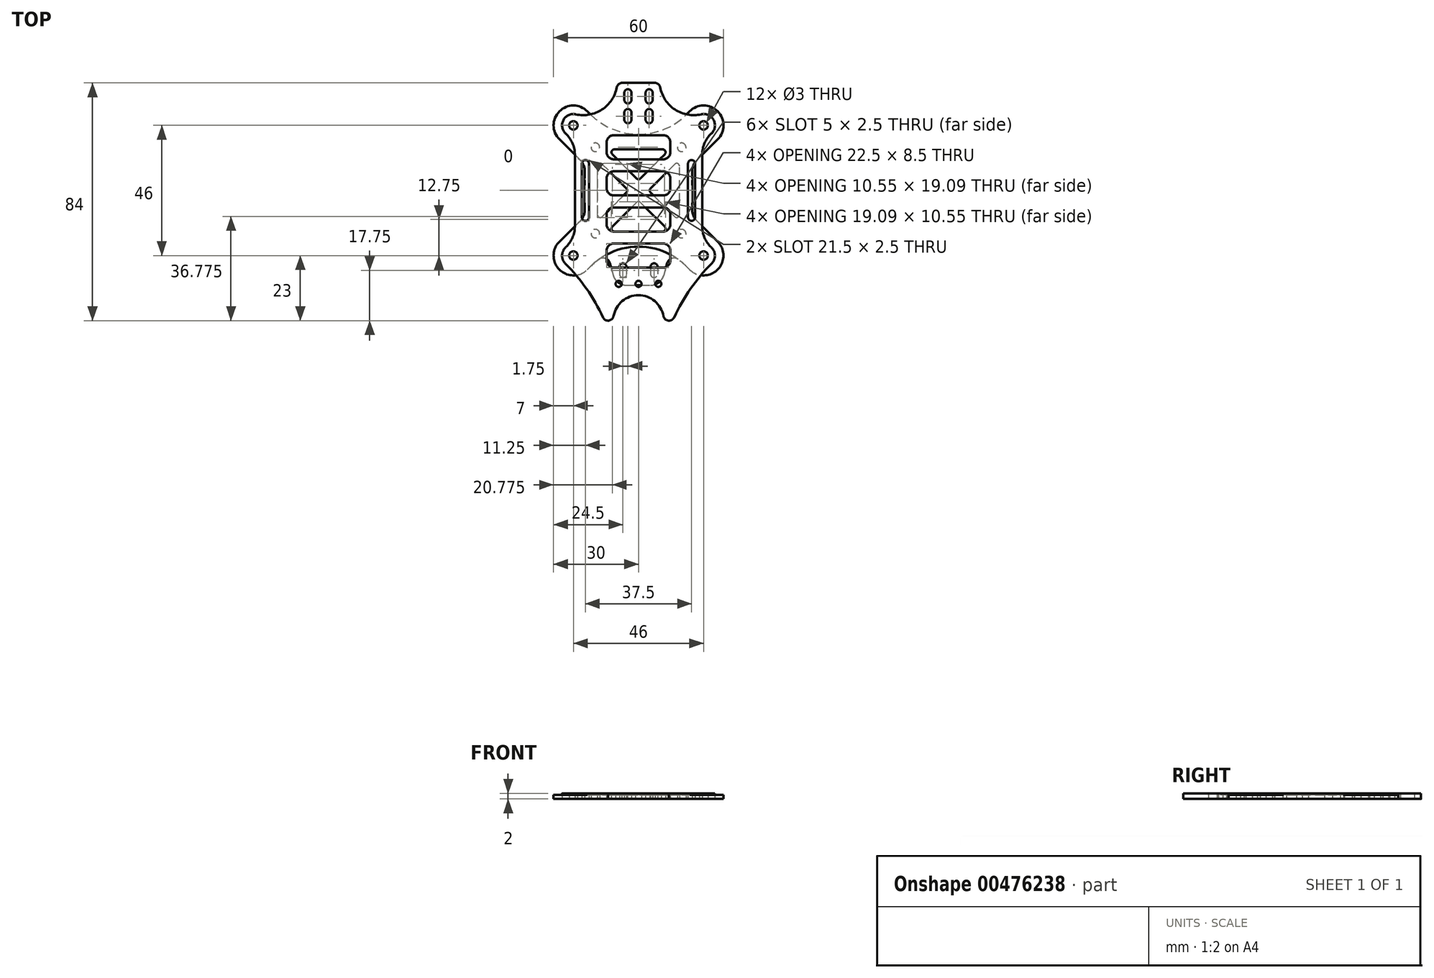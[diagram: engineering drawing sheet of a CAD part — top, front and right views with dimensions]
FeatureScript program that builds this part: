
annotation { "Feature Type Name" : "Feature", "Feature Type Description" : "" }
export const myFeature = defineFeature(function(context is Context, id is Id, definition is map)
    precondition{}
    {
        {
            var Q0;
            Q0=qCreatedBy(makeId("Top.planeOp"),FACE);
            var sketch = newSketch(context, id + "F0", { "sketchPlane" : qUnion([Q0])});
            skCircle(sketch, "E0", {"center": v(-15.25, 15.25) * mm, "radius": 1.52 * mm});
            skCircle(sketch, "E1", {"center": v(15.25, 15.25) * mm, "radius": 1.52 * mm});
            skCircle(sketch, "E2", {"center": v(15.25, -15.25) * mm, "radius": 1.52 * mm});
            skCircle(sketch, "E3", {"center": v(-15.25, -15.25) * mm, "radius": 1.52 * mm});
            skCircle(sketch, "E4", {"center": v(-23, 23) * mm, "radius": 1.5 * mm});
            skCircle(sketch, "E5.MirrorC", {"center": v(23, 23) * mm, "radius": 1.5 * mm});
            skCircle(sketch, "E6.MirrorC", {"center": v(-23, -23) * mm, "radius": 1.5 * mm});
            skCircle(sketch, "E7.MirrorC", {"center": v(23, -23) * mm, "radius": 1.5 * mm});
            skArc(sketch, "E8", {"start": v(-18.05, 27.95) * mm, "mid": v(-27.95, 27.95) * mm, "end": v(-27.95, 18.05) * mm});
            skLineSegment(sketch, "E9", {"start": v(-19, 7.03) * mm, "end": v(-19, -7.03) * mm});
            skLineSegment(sketch, "E10", {"start": v(-18.05, 27.95) * mm, "end": v(-16.97, 26.87) * mm});
            skLineSegment(sketch, "E11", {"start": v(-27.95, 18.05) * mm, "end": v(-20.46, 10.56) * mm});
            skLineSegment(sketch, "E12.MirrorCS", {"start": v(-27.95, -18.05) * mm, "end": v(-20.46, -10.56) * mm});
            skArc(sketch, "E13.MirrorCS", {"start": v(-18.05, -27.95) * mm, "mid": v(-27.95, -27.95) * mm, "end": v(-27.95, -18.05) * mm});
            skLineSegment(sketch, "E14.MirrorCS", {"start": v(-18.05, -27.95) * mm, "end": v(-16.97, -26.87) * mm});
            skLineSegment(sketch, "E15.MirrorCS", {"start": v(18.05, 27.95) * mm, "end": v(16.97, 26.87) * mm});
            skArc(sketch, "E16.MirrorCS", {"start": v(18.05, 27.95) * mm, "mid": v(27.95, 27.95) * mm, "end": v(27.95, 18.05) * mm});
            skLineSegment(sketch, "E17.MirrorCS", {"start": v(27.95, 18.05) * mm, "end": v(20.46, 10.56) * mm});
            skLineSegment(sketch, "E18.MirrorCS", {"start": v(27.95, -18.05) * mm, "end": v(20.46, -10.56) * mm});
            skArc(sketch, "E19.MirrorCS", {"start": v(18.05, -27.95) * mm, "mid": v(27.95, -27.95) * mm, "end": v(27.95, -18.05) * mm});
            skLineSegment(sketch, "E20.MirrorCS", {"start": v(18.05, -27.95) * mm, "end": v(16.97, -26.87) * mm});
            skPoint(sketch, "E21.visualSharp", {"position": v(0, 9.9) * mm});
            skPoint(sketch, "E22.visualSharp", {"position": v(0, -9.9) * mm});
            skArc(sketch, "E22.filletArc", {"start": v(16.97, -26.87) * mm, "mid": v(0, -19.84) * mm, "end": v(-16.97, -26.87) * mm});
            skLineSegment(sketch, "E23", {"start": v(-23, 23) * mm, "end": v(0, 0) * mm, "construction": true});
            skArc(sketch, "E24.filletArc", {"start": v(-16.97, 26.87) * mm, "mid": v(0, 19.84) * mm, "end": v(16.97, 26.87) * mm});
            skPoint(sketch, "E25.visualSharp", {"position": v(-19, 11.8) * mm});
            skArc(sketch, "E25.filletArc", {"start": v(-19, 7.03) * mm, "mid": v(-19.38, 8.94) * mm, "end": v(-20.46, 10.56) * mm});
            skPoint(sketch, "E26.visualSharp", {"position": v(-19, -11.8) * mm});
            skArc(sketch, "E26.filletArc", {"start": v(-20.46, -10.56) * mm, "mid": v(-19.38, -8.94) * mm, "end": v(-19, -7.03) * mm});
            skArc(sketch, "E27.MirrorCS", {"start": v(20.46, -10.56) * mm, "mid": v(19.38, -8.94) * mm, "end": v(19, -7.03) * mm});
            skArc(sketch, "E28.MirrorCS", {"start": v(19, 7.03) * mm, "mid": v(19.38, 8.94) * mm, "end": v(20.46, 10.56) * mm});
            skPoint(sketch, "E29.MirrorP", {"position": v(19, -11.8) * mm});
            skLineSegment(sketch, "E30.MirrorCS", {"start": v(19, 7.03) * mm, "end": v(19, -7.03) * mm});
            skPoint(sketch, "E31.MirrorP", {"position": v(21.5, -11.8) * mm});
            skPoint(sketch, "E32.MirrorP", {"position": v(21.5, 11.8) * mm});
            skPoint(sketch, "E33.MirrorP", {"position": v(19, 11.8) * mm});
            skLineSegment(sketch, "E34", {"start": v(0, 0) * mm, "end": v(23, -23) * mm, "construction": true});
            skLineSegment(sketch, "E35", {"start": v(23, 23) * mm, "end": v(-23, -23) * mm, "construction": true});
            skLineSegment(sketch, "E36.0", {"start": v(0.7, -4.24) * mm, "end": v(9.26, -12.8) * mm});
            skLineSegment(sketch, "E36.1", {"start": v(-12.8, 9.26) * mm, "end": v(-4.24, 0.7) * mm});
            skLineSegment(sketch, "E37.0", {"start": v(-9.26, 12.8) * mm, "end": v(-0.7, 4.24) * mm});
            skLineSegment(sketch, "E38.0", {"start": v(4.24, -0.7) * mm, "end": v(12.8, -9.26) * mm});
            skLineSegment(sketch, "E39.MirrorCS", {"start": v(9.26, 12.8) * mm, "end": v(0.7, 4.24) * mm});
            skLineSegment(sketch, "E40.MirrorCS", {"start": v(12.8, 9.26) * mm, "end": v(4.24, 0.7) * mm});
            skLineSegment(sketch, "E41.MirrorCS", {"start": v(-0.7, -4.24) * mm, "end": v(-9.26, -12.8) * mm});
            skLineSegment(sketch, "E42.MirrorCS", {"start": v(-4.24, -0.7) * mm, "end": v(-12.8, -9.26) * mm});
            skPoint(sketch, "E43.orphan", {"position": v(-1.77, -1.77) * mm});
            skPoint(sketch, "E44.orphan", {"position": v(1.77, -1.77) * mm});
            skLineSegment(sketch, "E45", {"start": v(-8.55, 14.5) * mm, "end": v(8.55, 14.5) * mm});
            skLineSegment(sketch, "E46", {"start": v(-14.5, 8.55) * mm, "end": v(-14.5, -8.55) * mm});
            skLineSegment(sketch, "E47", {"start": v(-8.55, -14.5) * mm, "end": v(8.55, -14.5) * mm});
            skLineSegment(sketch, "E48", {"start": v(14.5, -8.55) * mm, "end": v(14.5, 8.55) * mm});
            skPoint(sketch, "E49.visualSharp", {"position": v(-14.5, 10.96) * mm});
            skArc(sketch, "E49.filletArc", {"start": v(-12.8, 9.26) * mm, "mid": v(-13.88, 9.47) * mm, "end": v(-14.5, 8.55) * mm});
            skPoint(sketch, "E50.visualSharp", {"position": v(-14.5, -10.96) * mm});
            skArc(sketch, "E50.filletArc", {"start": v(-14.5, -8.55) * mm, "mid": v(-13.88, -9.47) * mm, "end": v(-12.8, -9.26) * mm});
            skPoint(sketch, "E51.visualSharp", {"position": v(-3.54, 0) * mm});
            skArc(sketch, "E51.filletArc", {"start": v(-4.24, -0.7) * mm, "mid": v(-3.95, 0) * mm, "end": v(-4.24, 0.7) * mm});
            skPoint(sketch, "E52.visualSharp", {"position": v(0, -3.54) * mm});
            skArc(sketch, "E52.filletArc", {"start": v(0.7, -4.24) * mm, "mid": v(0, -3.95) * mm, "end": v(-0.7, -4.24) * mm});
            skPoint(sketch, "E53.visualSharp", {"position": v(-10.96, -14.5) * mm});
            skArc(sketch, "E53.filletArc", {"start": v(-9.26, -12.8) * mm, "mid": v(-9.47, -13.88) * mm, "end": v(-8.55, -14.5) * mm});
            skPoint(sketch, "E54.visualSharp", {"position": v(10.96, -14.5) * mm});
            skArc(sketch, "E54.filletArc", {"start": v(8.55, -14.5) * mm, "mid": v(9.47, -13.88) * mm, "end": v(9.26, -12.8) * mm});
            skPoint(sketch, "E55.visualSharp", {"position": v(14.5, -10.96) * mm});
            skArc(sketch, "E55.filletArc", {"start": v(12.8, -9.26) * mm, "mid": v(13.88, -9.47) * mm, "end": v(14.5, -8.55) * mm});
            skPoint(sketch, "E56.visualSharp", {"position": v(14.5, 10.96) * mm});
            skArc(sketch, "E56.filletArc", {"start": v(14.5, 8.55) * mm, "mid": v(13.88, 9.47) * mm, "end": v(12.8, 9.26) * mm});
            skPoint(sketch, "E57.visualSharp", {"position": v(3.54, 0) * mm});
            skArc(sketch, "E57.filletArc", {"start": v(4.24, 0.7) * mm, "mid": v(3.95, 0) * mm, "end": v(4.24, -0.7) * mm});
            skPoint(sketch, "E58.visualSharp", {"position": v(0, 3.54) * mm});
            skArc(sketch, "E58.filletArc", {"start": v(-0.7, 4.24) * mm, "mid": v(0, 3.95) * mm, "end": v(0.7, 4.24) * mm});
            skPoint(sketch, "E59.visualSharp", {"position": v(-10.96, 14.5) * mm});
            skArc(sketch, "E59.filletArc", {"start": v(-8.55, 14.5) * mm, "mid": v(-9.47, 13.88) * mm, "end": v(-9.26, 12.8) * mm});
            skPoint(sketch, "E60.visualSharp", {"position": v(10.96, 14.5) * mm});
            skArc(sketch, "E60.filletArc", {"start": v(9.26, 12.8) * mm, "mid": v(9.47, 13.88) * mm, "end": v(8.55, 14.5) * mm});
            skLineSegment(sketch, "E61", {"start": v(-11, -22.5) * mm, "end": v(-9, -29.82) * mm});
            skLineSegment(sketch, "E62", {"start": v(-4.18, -33.5) * mm, "end": v(4.18, -33.5) * mm});
            skLineSegment(sketch, "E63", {"start": v(9, -29.82) * mm, "end": v(11, -22.5) * mm});
            skPoint(sketch, "E64.visualSharp", {"position": v(-8, -33.5) * mm});
            skArc(sketch, "E64.filletArc", {"start": v(-9, -29.82) * mm, "mid": v(-7.22, -32.47) * mm, "end": v(-4.18, -33.5) * mm});
            skPoint(sketch, "E65.visualSharp", {"position": v(8, -33.5) * mm});
            skArc(sketch, "E65.filletArc", {"start": v(4.18, -33.5) * mm, "mid": v(7.22, -32.47) * mm, "end": v(9, -29.82) * mm});
            skLineSegment(sketch, "E66", {"start": v(-5.5, -27) * mm, "end": v(-5.5, -29.5) * mm, "construction": true});
            skArc(sketch, "E67.0.startCap", {"start": v(-6.75, -27) * mm, "mid": v(-5.5, -25.75) * mm, "end": v(-4.25, -27) * mm});
            skArc(sketch, "E67.0.endCap", {"start": v(-4.25, -29.5) * mm, "mid": v(-5.5, -30.75) * mm, "end": v(-6.75, -29.5) * mm});
            skLineSegment(sketch, "E67.0.left", {"start": v(-4.25, -27) * mm, "end": v(-4.25, -29.5) * mm});
            skLineSegment(sketch, "E67.0.right", {"start": v(-6.75, -27) * mm, "end": v(-6.75, -29.5) * mm});
            skArc(sketch, "E68.MirrorCS", {"start": v(6.75, -27) * mm, "mid": v(5.5, -25.75) * mm, "end": v(4.25, -27) * mm});
            skArc(sketch, "E69.MirrorCS", {"start": v(4.25, -29.5) * mm, "mid": v(5.5, -30.75) * mm, "end": v(6.75, -29.5) * mm});
            skLineSegment(sketch, "E70.MirrorCS", {"start": v(5.5, -27) * mm, "end": v(5.5, -29.5) * mm, "construction": true});
            skLineSegment(sketch, "E71.MirrorCS", {"start": v(4.25, -27) * mm, "end": v(4.25, -29.5) * mm});
            skLineSegment(sketch, "E72.MirrorCS", {"start": v(6.75, -27) * mm, "end": v(6.75, -29.5) * mm});
            skSolve(sketch);
        }
        {
            var Q0;
            Q0=makeQuery(id+"F0.imprint","IMPRINT",FACE,{"disambiguationData":[TD([[makeQuery(id+"F0.imprint","IMPRINT",EDGE,{"derivedFrom":sQuery(id+"F0.wireOp",EDGE,"E0")}),-1.0]])]});
            extrude(context, id + "F1", {"entities" : qUnion([Q0]), "depth" : 1.5 * mm});
        }
        {
            var Q0;
            Q0 = qSketchRegion(id + "F0", true);
            extrude(context, id + "F2", {"entities" : qUnion([Q0]), "depth" : 1.5 * mm, "offsetDistance" : 25 * mm});
        }
        {
            var Q0;
            Q0=makeQuery(id+"F2.opExtrude","SWEPT_EDGE",EDGE,{"disambiguationData":[OSD([sQuery(id+"F0.wireOp",EDGE,"E22.filletArc"),sQuery(id+"F0.wireOp",EDGE,"E61")])]});
            var Q1;
            Q1=makeQuery(id+"F2.opExtrude","SWEPT_EDGE",EDGE,{"disambiguationData":[OSD([sQuery(id+"F0.wireOp",EDGE,"E22.filletArc"),sQuery(id+"F0.wireOp",EDGE,"E63")])]});
            fillet(context, id + "F3", {"entities" : qUnion([Q0, Q1]), "radius" : 2.5 * mm, "tangentPropagation" : true, "allowEdgeOverflow" : false});
        }
        {
            var Q0;
            Q0=qCreatedBy(makeId("Top.planeOp"),FACE);
            var sketch = newSketch(context, id + "F4", { "sketchPlane" : qUnion([Q0])});
            skCircle(sketch, "E73", {"center": v(-23, 23) * mm, "radius": 1.5 * mm});
            skLineSegment(sketch, "E74", {"start": v(-23, 23) * mm, "end": v(0, 0) * mm, "construction": true});
            skLineSegment(sketch, "E75", {"start": v(-22.5, 12.72) * mm, "end": v(-22.5, 0) * mm});
            skArc(sketch, "E76.filletArc", {"start": v(-22.5, 12.72) * mm, "mid": v(-23.34, 16.73) * mm, "end": v(-25.71, 20.06) * mm});
            skLineSegment(sketch, "E77", {"start": v(0, 0) * mm, "end": v(0, 0) * mm});
            skLineSegment(sketch, "E78.MirrorCS", {"start": v(22.5, 12.72) * mm, "end": v(22.5, 0) * mm});
            skCircle(sketch, "E79.MirrorC", {"center": v(23, 23) * mm, "radius": 1.5 * mm});
            skLineSegment(sketch, "E80.MirrorCS", {"start": v(23, 23) * mm, "end": v(0, 0) * mm, "construction": true});
            skArc(sketch, "E81.MirrorCS", {"start": v(22.5, 12.72) * mm, "mid": v(23.34, 16.73) * mm, "end": v(25.71, 20.06) * mm});
            skLineSegment(sketch, "E82.MirrorCS", {"start": v(0, 36) * mm, "end": v(0, 0) * mm, "construction": true});
            skArc(sketch, "E83.MirrorCS", {"start": v(-22.5, -12.72) * mm, "mid": v(-23.34, -16.73) * mm, "end": v(-25.71, -20.06) * mm});
            skLineSegment(sketch, "E84.MirrorCS", {"start": v(-22.5, -12.72) * mm, "end": v(-22.5, 0) * mm});
            skLineSegment(sketch, "E85.MirrorCS", {"start": v(22.5, -12.72) * mm, "end": v(22.5, 0) * mm});
            skArc(sketch, "E86.MirrorCS", {"start": v(22.5, -12.72) * mm, "mid": v(23.34, -16.73) * mm, "end": v(25.71, -20.06) * mm});
            skArc(sketch, "E87.MirrorCS", {"start": v(25.83, -25.83) * mm, "mid": v(27, -22.92) * mm, "end": v(25.71, -20.06) * mm});
            skCircle(sketch, "E88.MirrorC", {"center": v(-23, -23) * mm, "radius": 1.5 * mm});
            skCircle(sketch, "E89.MirrorC", {"center": v(23, -23) * mm, "radius": 1.5 * mm});
            skLineSegment(sketch, "E90", {"start": v(0, 0) * mm, "end": v(-72.48, -72.48) * mm, "construction": true});
            skCircle(sketch, "E91", {"center": v(-72.48, -72.48) * mm, "radius": 65.25 * mm, "construction": true});
            skArc(sketch, "E92", {"start": v(-12.05, -46) * mm, "mid": v(-18, -35.27) * mm, "end": v(-25.83, -25.83) * mm});
            skArc(sketch, "E93", {"start": v(-25.83, -25.83) * mm, "mid": v(-27, -22.92) * mm, "end": v(-25.71, -20.06) * mm});
            skArc(sketch, "E94.MirrorCS", {"start": v(12.05, -46) * mm, "mid": v(18, -35.27) * mm, "end": v(25.83, -25.83) * mm});
            skLineSegment(sketch, "E95", {"start": v(-12.05, -46) * mm, "end": v(-8.97, -46) * mm});
            skLineSegment(sketch, "E96.trimOffspring", {"start": v(8.97, -46) * mm, "end": v(12.05, -46) * mm});
            skLineSegment(sketch, "E97", {"start": v(-3.75, 27.5) * mm, "end": v(-3.75, 25) * mm, "construction": true});
            skArc(sketch, "E98.0.startCap", {"start": v(-5, 27.5) * mm, "mid": v(-3.75, 28.75) * mm, "end": v(-2.5, 27.5) * mm});
            skArc(sketch, "E98.0.endCap", {"start": v(-2.5, 25) * mm, "mid": v(-3.75, 23.75) * mm, "end": v(-5, 25) * mm});
            skLineSegment(sketch, "E98.0.left", {"start": v(-2.5, 27.5) * mm, "end": v(-2.5, 25) * mm});
            skLineSegment(sketch, "E98.0.right", {"start": v(-5, 27.5) * mm, "end": v(-5, 25) * mm});
            skLineSegment(sketch, "E99.MirrorCS", {"start": v(5, 27.5) * mm, "end": v(5, 25) * mm});
            skArc(sketch, "E100.MirrorCS", {"start": v(5, 27.5) * mm, "mid": v(3.75, 28.75) * mm, "end": v(2.5, 27.5) * mm});
            skArc(sketch, "E101.MirrorCS", {"start": v(2.5, 25) * mm, "mid": v(3.75, 23.75) * mm, "end": v(5, 25) * mm});
            skLineSegment(sketch, "E102.MirrorCS", {"start": v(2.5, 27.5) * mm, "end": v(2.5, 25) * mm});
            skLineSegment(sketch, "E103.MirrorCS", {"start": v(3.75, 27.5) * mm, "end": v(3.75, 25) * mm, "construction": true});
            skLineSegment(sketch, "E104", {"start": v(-5.73, 38) * mm, "end": v(5.73, 38) * mm});
            skArc(sketch, "E105", {"start": v(-25.71, 20.06) * mm, "mid": v(-26.54, 24.86) * mm, "end": v(-22.12, 26.9) * mm});
            skArc(sketch, "E106", {"start": v(25.71, 20.06) * mm, "mid": v(26.54, 24.86) * mm, "end": v(22.12, 26.9) * mm});
            skArc(sketch, "E107", {"start": v(-22.12, 26.9) * mm, "mid": v(-12.9, 28.58) * mm, "end": v(-7.7, 36.37) * mm});
            skArc(sketch, "E108.MirrorCS", {"start": v(22.12, 26.9) * mm, "mid": v(12.9, 28.58) * mm, "end": v(7.7, 36.37) * mm});
            skArc(sketch, "E109", {"start": v(8.97, -46) * mm, "mid": v(0, -37.03) * mm, "end": v(-8.97, -46) * mm});
            skPoint(sketch, "E110.visualSharp", {"position": v(-7.5, 38) * mm});
            skArc(sketch, "E110.filletArc", {"start": v(-5.73, 38) * mm, "mid": v(-7, 37.54) * mm, "end": v(-7.7, 36.37) * mm});
            skPoint(sketch, "E111.visualSharp", {"position": v(7.5, 38) * mm});
            skArc(sketch, "E111.filletArc", {"start": v(7.7, 36.37) * mm, "mid": v(7, 37.54) * mm, "end": v(5.73, 38) * mm});
            skArc(sketch, "E112.0.1.0", {"start": v(2.5, 32) * mm, "mid": v(3.75, 30.75) * mm, "end": v(5, 32) * mm});
            skLineSegment(sketch, "E112.0.1.1", {"start": v(3.75, 34.5) * mm, "end": v(3.75, 32) * mm, "construction": true});
            skArc(sketch, "E112.0.1.2", {"start": v(5, 34.5) * mm, "mid": v(3.75, 35.75) * mm, "end": v(2.5, 34.5) * mm});
            skLineSegment(sketch, "E112.0.1.3", {"start": v(5, 34.5) * mm, "end": v(5, 32) * mm});
            skLineSegment(sketch, "E112.0.1.4", {"start": v(-2.5, 34.5) * mm, "end": v(-2.5, 32) * mm});
            skLineSegment(sketch, "E112.0.1.5", {"start": v(-3.75, 34.5) * mm, "end": v(-3.75, 32) * mm, "construction": true});
            skArc(sketch, "E112.0.1.6", {"start": v(-2.5, 32) * mm, "mid": v(-3.75, 30.75) * mm, "end": v(-5, 32) * mm});
            skLineSegment(sketch, "E112.0.1.7", {"start": v(2.5, 34.5) * mm, "end": v(2.5, 32) * mm});
            skLineSegment(sketch, "E112.0.1.8", {"start": v(-5, 34.5) * mm, "end": v(-5, 32) * mm});
            skArc(sketch, "E112.0.1.9", {"start": v(-5, 34.5) * mm, "mid": v(-3.75, 35.75) * mm, "end": v(-2.5, 34.5) * mm});
            skLineSegment(sketch, "E112.direction1", {"start": v(-5, 25) * mm, "end": v(20, 25) * mm, "construction": true});
            skLineSegment(sketch, "E112.direction2", {"start": v(-5, 25) * mm, "end": v(-5, 32) * mm, "construction": true});
            skCircle(sketch, "E113", {"center": v(-7, -33) * mm, "radius": 1.07 * mm});
            skCircle(sketch, "E114.MirrorC", {"center": v(7, -33) * mm, "radius": 1.07 * mm});
            skCircle(sketch, "E115", {"center": v(0, -33) * mm, "radius": 1.07 * mm});
            skLineSegment(sketch, "E116", {"start": v(-18.75, 9.5) * mm, "end": v(-18.75, -9.5) * mm, "construction": true});
            skArc(sketch, "E117.0.startCap", {"start": v(-20, 9.5) * mm, "mid": v(-18.75, 10.75) * mm, "end": v(-17.5, 9.5) * mm});
            skArc(sketch, "E117.0.endCap", {"start": v(-17.5, -9.5) * mm, "mid": v(-18.75, -10.75) * mm, "end": v(-20, -9.5) * mm});
            skLineSegment(sketch, "E117.0.left", {"start": v(-17.5, 9.5) * mm, "end": v(-17.5, -9.5) * mm});
            skLineSegment(sketch, "E117.0.right", {"start": v(-20, 9.5) * mm, "end": v(-20, -9.5) * mm});
            skLineSegment(sketch, "E118.MirrorCS", {"start": v(18.75, 9.5) * mm, "end": v(18.75, -9.5) * mm, "construction": true});
            skLineSegment(sketch, "E119.MirrorCS", {"start": v(17.5, 9.5) * mm, "end": v(17.5, -9.5) * mm});
            skArc(sketch, "E120.MirrorCS", {"start": v(17.5, -9.5) * mm, "mid": v(18.75, -10.75) * mm, "end": v(20, -9.5) * mm});
            skArc(sketch, "E121.MirrorCS", {"start": v(20, 9.5) * mm, "mid": v(18.75, 10.75) * mm, "end": v(17.5, 9.5) * mm});
            skLineSegment(sketch, "E122.MirrorCS", {"start": v(20, 9.5) * mm, "end": v(20, -9.5) * mm});
            skLineSegment(sketch, "E123.bottom", {"start": v(-8.75, 19.5) * mm, "end": v(8.75, 19.5) * mm});
            skLineSegment(sketch, "E123.top", {"start": v(-8.75, 11) * mm, "end": v(8.75, 11) * mm});
            skLineSegment(sketch, "E123.left", {"start": v(-11.25, 17) * mm, "end": v(-11.25, 13.5) * mm});
            skLineSegment(sketch, "E123.right", {"start": v(11.25, 17) * mm, "end": v(11.25, 13.5) * mm});
            skPoint(sketch, "E124.visualSharp", {"position": v(-11.25, 19.5) * mm});
            skArc(sketch, "E124.filletArc", {"start": v(-8.75, 19.5) * mm, "mid": v(-10.52, 18.77) * mm, "end": v(-11.25, 17) * mm});
            skPoint(sketch, "E125.visualSharp", {"position": v(-11.25, 11) * mm});
            skArc(sketch, "E125.filletArc", {"start": v(-11.25, 13.5) * mm, "mid": v(-10.52, 11.73) * mm, "end": v(-8.75, 11) * mm});
            skPoint(sketch, "E126.visualSharp", {"position": v(11.25, 11) * mm});
            skArc(sketch, "E126.filletArc", {"start": v(8.75, 11) * mm, "mid": v(10.52, 11.73) * mm, "end": v(11.25, 13.5) * mm});
            skPoint(sketch, "E127.visualSharp", {"position": v(11.25, 19.5) * mm});
            skArc(sketch, "E127.filletArc", {"start": v(11.25, 17) * mm, "mid": v(10.52, 18.77) * mm, "end": v(8.75, 19.5) * mm});
            skLineSegment(sketch, "E128.0.1.0", {"start": v(-11.25, 4.25) * mm, "end": v(-11.25, 0.75) * mm});
            skLineSegment(sketch, "E128.0.1.1", {"start": v(-8.75, 6.75) * mm, "end": v(8.75, 6.75) * mm});
            skPoint(sketch, "E128.0.1.2", {"position": v(11.25, 6.75) * mm});
            skLineSegment(sketch, "E128.0.1.3", {"start": v(-8.75, -1.75) * mm, "end": v(8.75, -1.75) * mm});
            skPoint(sketch, "E128.0.1.4", {"position": v(11.25, -1.75) * mm});
            skPoint(sketch, "E128.0.1.5", {"position": v(-11.25, 6.75) * mm});
            skLineSegment(sketch, "E128.0.1.6", {"start": v(11.25, 4.25) * mm, "end": v(11.25, 0.75) * mm});
            skPoint(sketch, "E128.0.1.7", {"position": v(-11.25, -1.75) * mm});
            skArc(sketch, "E128.0.1.8", {"start": v(8.75, -1.75) * mm, "mid": v(10.52, -1.02) * mm, "end": v(11.25, 0.75) * mm});
            skArc(sketch, "E128.0.1.9", {"start": v(11.25, 4.25) * mm, "mid": v(10.52, 6.02) * mm, "end": v(8.75, 6.75) * mm});
            skArc(sketch, "E128.0.1.10", {"start": v(-8.75, 6.75) * mm, "mid": v(-10.52, 6.02) * mm, "end": v(-11.25, 4.25) * mm});
            skArc(sketch, "E128.0.1.11", {"start": v(-11.25, 0.75) * mm, "mid": v(-10.52, -1.02) * mm, "end": v(-8.75, -1.75) * mm});
            skLineSegment(sketch, "E128.0.2.0", {"start": v(-11.25, -8.5) * mm, "end": v(-11.25, -12) * mm});
            skLineSegment(sketch, "E128.0.2.1", {"start": v(-8.75, -6) * mm, "end": v(8.75, -6) * mm});
            skPoint(sketch, "E128.0.2.2", {"position": v(11.25, -6) * mm});
            skLineSegment(sketch, "E128.0.2.3", {"start": v(-8.75, -14.5) * mm, "end": v(8.75, -14.5) * mm});
            skPoint(sketch, "E128.0.2.4", {"position": v(11.25, -14.5) * mm});
            skPoint(sketch, "E128.0.2.5", {"position": v(-11.25, -6) * mm});
            skLineSegment(sketch, "E128.0.2.6", {"start": v(11.25, -8.5) * mm, "end": v(11.25, -12) * mm});
            skPoint(sketch, "E128.0.2.7", {"position": v(-11.25, -14.5) * mm});
            skArc(sketch, "E128.0.2.8", {"start": v(8.75, -14.5) * mm, "mid": v(10.52, -13.77) * mm, "end": v(11.25, -12) * mm});
            skArc(sketch, "E128.0.2.9", {"start": v(11.25, -8.5) * mm, "mid": v(10.52, -6.73) * mm, "end": v(8.75, -6) * mm});
            skArc(sketch, "E128.0.2.10", {"start": v(-8.75, -6) * mm, "mid": v(-10.52, -6.73) * mm, "end": v(-11.25, -8.5) * mm});
            skArc(sketch, "E128.0.2.11", {"start": v(-11.25, -12) * mm, "mid": v(-10.52, -13.77) * mm, "end": v(-8.75, -14.5) * mm});
            skLineSegment(sketch, "E128.0.3.0", {"start": v(-11.25, -21.25) * mm, "end": v(-11.25, -24.75) * mm});
            skLineSegment(sketch, "E128.0.3.1", {"start": v(-8.75, -18.75) * mm, "end": v(8.75, -18.75) * mm});
            skPoint(sketch, "E128.0.3.2", {"position": v(11.25, -18.75) * mm});
            skLineSegment(sketch, "E128.0.3.3", {"start": v(-8.75, -27.25) * mm, "end": v(8.75, -27.25) * mm});
            skPoint(sketch, "E128.0.3.4", {"position": v(11.25, -27.25) * mm});
            skPoint(sketch, "E128.0.3.5", {"position": v(-11.25, -18.75) * mm});
            skLineSegment(sketch, "E128.0.3.6", {"start": v(11.25, -21.25) * mm, "end": v(11.25, -24.75) * mm});
            skPoint(sketch, "E128.0.3.7", {"position": v(-11.25, -27.25) * mm});
            skArc(sketch, "E128.0.3.8", {"start": v(8.75, -27.25) * mm, "mid": v(10.52, -26.52) * mm, "end": v(11.25, -24.75) * mm});
            skArc(sketch, "E128.0.3.9", {"start": v(11.25, -21.25) * mm, "mid": v(10.52, -19.48) * mm, "end": v(8.75, -18.75) * mm});
            skArc(sketch, "E128.0.3.10", {"start": v(-8.75, -18.75) * mm, "mid": v(-10.52, -19.48) * mm, "end": v(-11.25, -21.25) * mm});
            skArc(sketch, "E128.0.3.11", {"start": v(-11.25, -24.75) * mm, "mid": v(-10.52, -26.52) * mm, "end": v(-8.75, -27.25) * mm});
            skLineSegment(sketch, "E128.direction1", {"start": v(-11.25, 11) * mm, "end": v(14, 11) * mm, "construction": true});
            skLineSegment(sketch, "E128.direction2", {"start": v(-11.25, 11) * mm, "end": v(-11.25, -1.75) * mm, "construction": true});
            skSolve(sketch);
        }
        {
            var Q0;
            Q0=makeQuery(id+"F4.imprint","IMPRINT",FACE,{"disambiguationData":[TD([[makeQuery(id+"F4.imprint","IMPRINT",EDGE,{"derivedFrom":sQuery(id+"F4.wireOp",EDGE,"E73")}),-1.0]])]});
            extrude(context, id + "F5", {"entities" : qUnion([Q0]), "offsetDistance" : 25 * mm, "depth" : 2 * mm});
        }
        {
            var Q0;
            Q0=makeQuery(id+"F5.opExtrude","SWEPT_EDGE",EDGE,{"disambiguationData":[OSD([sQuery(id+"F4.wireOp",EDGE,"E92"),sQuery(id+"F4.wireOp",EDGE,"E95")])]});
            var Q1;
            Q1=makeQuery(id+"F5.opExtrude","SWEPT_EDGE",EDGE,{"disambiguationData":[OSD([sQuery(id+"F4.wireOp",EDGE,"E95"),sQuery(id+"F4.wireOp",EDGE,"E109")])]});
            var Q2;
            Q2=makeQuery(id+"F5.opExtrude","SWEPT_EDGE",EDGE,{"disambiguationData":[OSD([sQuery(id+"F4.wireOp",EDGE,"E96.trimOffspring"),sQuery(id+"F4.wireOp",EDGE,"E109")])]});
            var Q3;
            Q3=makeQuery(id+"F5.opExtrude","SWEPT_EDGE",EDGE,{"disambiguationData":[OSD([sQuery(id+"F4.wireOp",EDGE,"E94.MirrorCS"),sQuery(id+"F4.wireOp",EDGE,"E96.trimOffspring")])]});
            fillet(context, id + "F6", {"entities" : qUnion([Q0, Q1, Q2, Q3]), "radius" : 2 * mm, "tangentPropagation" : true, "allowEdgeOverflow" : false});
        }
    });
